# Revit family: Линкос_общий
name_source: partatom
category: Осветительные приборы
units: mm (PartAtom-declared; Revit-internal decimal feet)

## family parameters
Всегда вертикально = Да
Источник света = Да
На основе рабочей плоскости = Нет
Общий = Нет
При загрузке вырезать с полостями = Нет
Размер круглого соединителя = Использовать диаметр
Тип детали = Нормальный
Точка расчета площади = Нет

## types (12) — shared parameters
ADSK_URL страницы изделия = https://www.allfresco.ru
ADSK_Единица измерения = шт.
ADSK_Завод-изготовитель = ALFRESCO
ADSK_Количество фаз = 2
ADSK_Модель = Линкос ДТУ-126-AF
ADSK_Напряжение = 220 В
ADSK_Полная мощность = 0 В·А
ADSK_Ток = 0 А
ADSK_Энергоэффективность = 110 лм/Вт
D_профиль светильник = 89 мм
D_столб = 108 мм
D_фланец = 250 мм
H_верх дверки = 944 мм
H_конечной точки = 1500 мм
H_надстолбие = 200 мм
H_стобШапочка = 1 мм
H_фланец = 14 мм
IP Class = IP 67
L_ось светильника обратно = 136 мм
L_отступ до конечной точки = 1500 мм
L_отступ до центра = 1000 мм
R_дверка = 54 мм
a1_внутри светильнкиа = 39 мм
a2_внутри светильника = 200 мм
h_внутри светильника = 20 мм
h_дверка = 440 мм
Блок аварийного питания = Нет
Класс защиты = 1
Класс пожароопасности = F (светильники предназначены для установки непосредственно на поверхность из нормально воспламеняемых материалов)
Климатическая зона = УХЛ1
Короб_Диаметр = 20 мм
Корпус светильника = Сталь, окрашенная, темно-серая
Материал рассеивателя = Светотехнический ПК
Область использования = Парки, скверы, общественные пространства, городская инфраструктура
Полная установленная мощность = 0 В·А
Рассеиватель = Белый_Светодиод
Светофильтр = 16777215
Смещение цветовой температуры при затухании лампы = <Нет>
Таблица выбора = Таблица параметров светильников_par3_v1
Температура эксплуатации = -40 +50
Тип ИС = LED-модуль
Тип КСС = тип ШБ (широкая боковая)
Тип ПРА = -
Тип продукции = LED-светильник
Угол наклона = 90.00°
Цветоывая температура = 2700-5500
zero-valued in all types: ADSK_Количество фаз числовое, ADSK_Коэффициент мощности

## per-type parameters (varying)
| type | ADSK_Артикул | ADSK_Масса | ADSK_Масса_Текст | ADSK_Наименование | ADSK_Номинальная мощность | ADSK_Размер_Высота | ADSK_Фактическая мощность | Angle | Angle_1 | H_ось поворота | H_столб | H_точки освещения | L_ось светильника | a_отступ точки освещения | Файл фотометрической сетки |
| ДТУ2v126с8 Светодиодный светильник Линкос ДТУ-126-AF-40Вт-4,0 | ДТУ2v126с8 | 45 | 45 | ДТУ2v126с8 Светодиодный светильник Линкос ДТУ-126-AF-40Вт-4.0 | 40 Вт | 4000 мм | 38 Вт | 10.00° | 0.00° | 100 мм | 3804 мм | 70 мм | 1070 мм | 870 мм | DTU-126-AF Linkos 40W 146x60.ies |
| ДТУ2v126с9 Светодиодный светильник Линкос ДТУ-126-AF-60Вт-4,0 | ДТУ2v126с9 | 46 | 46 | ДТУ2v126с9 Светодиодный светильник Линкос ДТУ-126-AF-60Вт-4.0 | 60 Вт | 4000 мм | 59 Вт | 10.00° | 0.00° | 100 мм | 3804 мм | 70 мм | 1070 мм | 870 мм | DTU-126-AF Linkos 60W 146x60.ies |
| ДТУ2v126с5 Светодиодный светильник Линкос ДТУ-126-AF-40Вт-4,0-15гр | ДТУ2v126с5 | 46 | 46 | ДТУ2v126с5 Светодиодный светильник Линкос ДТУ-126-AF-40Вт-4.0-15гр | 40 Вт | 4000 мм | 38 Вт | 25.00° | 15.00° | 112 мм | 3804 мм | 310 мм | 1085 мм | 885 мм | DTU-126-AF Linkos 40W 146x60.ies |
| ДТУ2v126с6 Светодиодный светильник Линкос ДТУ-126-AF-60Вт-4,0-15гр | ДТУ2v126с6 | 47 | 47 | ДТУ2v126с6 Светодиодный светильник Линкос ДТУ-126-AF-60Вт-4.0-15гр | 60 Вт | 4000 мм | 59 Вт | 25.00° | 15.00° | 112 мм | 3804 мм | 310 мм | 1085 мм | 885 мм | DTU-126-AF Linkos 60W 146x60.ies |
| ДТУ2v126с10 Светодиодный светильник Линкос ДТУ-126-AF-40Вт-5,0 | ДТУ2v126с10 | 51 | 51 | ДТУ2v126с10 Светодиодный светильник Линкос ДТУ-126-AF-40Вт-5.0 | 40 Вт | 5000 мм | 38 Вт | 10.00° | 0.00° | 100 мм | 4804 мм | 70 мм | 1070 мм | 870 мм | DTU-126-AF Linkos 40W 146x60.ies |
| ДТУ2v126с11 Светодиодный светильник Линкос ДТУ-126-AF-60Вт-5,0 | ДТУ2v126с11 | 52 | 52 | ДТУ2v126с11 Светодиодный светильник Линкос ДТУ-126-AF-60Вт-5.0 | 60 Вт | 5000 мм | 59 Вт | 10.00° | 0.00° | 100 мм | 4804 мм | 70 мм | 1070 мм | 870 мм | DTU-126-AF Linkos 60W 146x60.ies |
| ДТУ2v126с12 Светодиодный светильник Линкос ДТУ-126-AF-40Вт-5,0-15гр | ДТУ2v126с12 | 52 | 52 | ДТУ2v126с12 Светодиодный светильник Линкос ДТУ-126-AF-40Вт-5.0-15гр | 40 Вт | 5000 мм | 38 Вт | 25.00° | 15.00° | 112 мм | 4804 мм | 310 мм | 1085 мм | 885 мм | DTU-126-AF Linkos 40W 146x60.ies |
| ДТУ2v126с13 Светодиодный светильник Линкос ДТУ-126-AF-60Вт-5,0-15гр | ДТУ2v126с13 | 53 | 53 | ДТУ2v126с13 Светодиодный светильник Линкос ДТУ-126-AF-60Вт-5.0-15гр | 60 Вт | 5000 мм | 59 Вт | 25.00° | 15.00° | 112 мм | 4804 мм | 310 мм | 1085 мм | 885 мм | DTU-126-AF Linkos 60W 146x60.ies |
| ДТУ2v126с14 Светодиодный светильник Линкос ДТУ-126-AF-40Вт-6,0 | ДТУ2v126с14 | 57 | 57 | ДТУ2v126с14 Светодиодный светильник Линкос ДТУ-126-AF-40Вт-6.0 | 40 Вт | 6000 мм | 38 Вт | 10.00° | 0.00° | 100 мм | 5804 мм | 70 мм | 1070 мм | 870 мм | DTU-126-AF Linkos 40W 146x60.ies |
| ДТУ2v126с15 Светодиодный светильник Линкос ДТУ-126-AF-60Вт-6,0 | ДТУ2v126с15 | 58 | 58 | ДТУ2v126с15 Светодиодный светильник Линкос ДТУ-126-AF-60Вт-6.0 | 60 Вт | 6000 мм | 59 Вт | 10.00° | 0.00° | 100 мм | 5804 мм | 70 мм | 1070 мм | 870 мм | DTU-126-AF Linkos 60W 146x60.ies |
| ДТУ2v126с16 Светодиодный светильник Линкос ДТУ-126-AF-40Вт-6,0-15гр | ДТУ2v126с16 | 58 | 58 | ДТУ2v126с16 Светодиодный светильник Линкос ДТУ-126-AF-40Вт-6.0-15гр | 40 Вт | 6000 мм | 38 Вт | 25.00° | 15.00° | 112 мм | 5804 мм | 310 мм | 1085 мм | 885 мм | DTU-126-AF Linkos 40W 146x60.ies |
| ДТУ2v126с17 Светодиодный светильник Линкос ДТУ-126-AF-60Вт-6,0-15гр | ДТУ2v126с17 | 59 | 59 | ДТУ2v126с17 Светодиодный светильник Линкос ДТУ-126-AF-60Вт-6.0-15гр | 60 Вт | 6000 мм | 59 Вт | 25.00° | 15.00° | 112 мм | 5804 мм | 310 мм | 1085 мм | 885 мм | DTU-126-AF Linkos 60W 146x60.ies |
